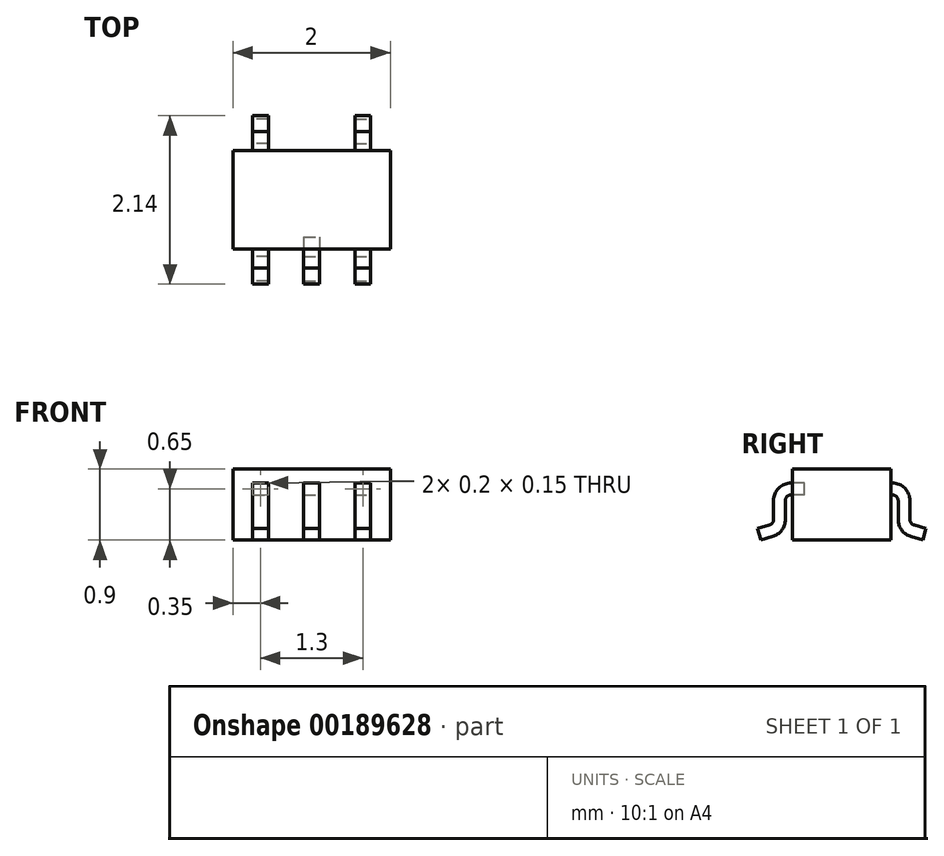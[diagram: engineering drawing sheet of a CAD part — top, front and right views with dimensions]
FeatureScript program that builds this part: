
annotation { "Feature Type Name" : "Feature", "Feature Type Description" : "" }
export const myFeature = defineFeature(function(context is Context, id is Id, definition is map)
    precondition{}
    {
        {
            var Q0;
            Q0=qCreatedBy(makeId("Top.planeOp"),FACE);
            var sketch = newSketch(context, id + "F0", { "sketchPlane" : qUnion([Q0])});
            skLineSegment(sketch, "E0.bottom", {"start": v(1, 0.62) * mm, "end": v(-1, 0.62) * mm});
            skLineSegment(sketch, "E0.top", {"start": v(1, -0.63) * mm, "end": v(-1, -0.63) * mm});
            skLineSegment(sketch, "E0.left", {"start": v(1, 0.62) * mm, "end": v(1, -0.63) * mm});
            skLineSegment(sketch, "E0.right", {"start": v(-1, 0.62) * mm, "end": v(-1, -0.63) * mm});
            skPoint(sketch, "E0.middle", {"position": v(0, 0) * mm});
            skSolve(sketch);
        }
        {
            var Q0;
            Q0=qSketchRegion(id+"F0",true);
            extrude(context, id + "F1", {"entities" : qUnion([Q0]), "depth" : 0.9 * mm});
        }
        {
            var Q0;
            Q0=qCreatedBy(makeId("Right.planeOp"),FACE);
            var sketch = newSketch(context, id + "F2", { "sketchPlane" : qUnion([Q0])});
            skLineSegment(sketch, "E1", {"start": v(-0.47, 0.65) * mm, "end": v(-0.64, 0.65) * mm});
            skLineSegment(sketch, "E2", {"start": v(-0.8, 0.5) * mm, "end": v(-0.8, 0.26) * mm});
            skLineSegment(sketch, "E3", {"start": v(-0.9, 0.12) * mm, "end": v(-1.05, 0.07) * mm});
            skPoint(sketch, "E4.visualSharp", {"position": v(-0.8, 0.65) * mm});
            skArc(sketch, "E4.filletArc", {"start": v(-0.64, 0.65) * mm, "mid": v(-0.75, 0.6) * mm, "end": v(-0.8, 0.5) * mm});
            skPoint(sketch, "E5.visualSharp", {"position": v(-0.8, 0.15) * mm});
            skArc(sketch, "E5.filletArc", {"start": v(-0.9, 0.12) * mm, "mid": v(-0.82, 0.17) * mm, "end": v(-0.8, 0.26) * mm});
            skSolve(sketch);
        }
        {
            var Q0;
            Q0=sQuery(id+"F2.wireOp",EDGE,"E1");
            var Q1;
            Q1=sQuery(id+"F2.wireOp",VERTEX,"E1.start");
            cPlane(context, id + "F3", {"entities" : qUnion([Q0, Q1]), "cplaneType" : CPlaneType.CURVE_POINT, "offset" : 150 * mm, "width" : 150 * mm, "height" : 150 * mm});
        }
        {
            var Q0;
            Q0=qCreatedBy(id+"F3.planeOp",FACE);
            var sketch = newSketch(context, id + "F4", { "sketchPlane" : qUnion([Q0])});
            skLineSegment(sketch, "E6.bottom", {"start": v(-0.1, 0.58) * mm, "end": v(0.1, 0.58) * mm});
            skLineSegment(sketch, "E6.top", {"start": v(-0.1, 0.73) * mm, "end": v(0.1, 0.73) * mm});
            skLineSegment(sketch, "E6.left", {"start": v(-0.1, 0.58) * mm, "end": v(-0.1, 0.73) * mm});
            skLineSegment(sketch, "E6.right", {"start": v(0.1, 0.58) * mm, "end": v(0.1, 0.73) * mm});
            skPoint(sketch, "E6.middle", {"position": v(0, 0.65) * mm});
            skSolve(sketch);
        }
        {
            var Q0;
            Q0=qSketchRegion(id+"F4",true);
            var Q1;
            Q1=qConstructionFilter(qBodyType(qCreatedBy(id+"F2",EDGE),BodyType.WIRE),ConstructionObject.NO);
            sweep(context, id + "F5", {"profiles" : qUnion([Q0]), "path" : qUnion([Q1])});
        }
        {
            var Q0;
            Q0=makeQuery(id+"F5.opSweep","SWEPT_BODY",BODY,{"disambiguationData":[OSD([sQuery(id+"F2.wireOp",EDGE,"E1"),sQuery(id+"F4.wireOp",EDGE,"E6.bottom"),sQuery(id+"F4.wireOp",EDGE,"E6.top"),sQuery(id+"F4.wireOp",EDGE,"E6.left"),sQuery(id+"F4.wireOp",EDGE,"E6.right")])]});
            transform(context, id + "F6", {"entities" : qUnion([Q0]), "transformType" : TransformType.TRANSLATION_3D, "dx" : 0.65 * mm, "dy" : 0 * mm, "dz" : 0 * mm, "makeCopy" : true});
        }
        {
            var Q0;
            Q0=makeQuery(id+"F6.opPattern","COPY",BODY,{"derivedFrom":makeQuery(id+"F5.opSweep","SWEPT_BODY",BODY,{"disambiguationData":[OSD([sQuery(id+"F2.wireOp",EDGE,"E1"),sQuery(id+"F4.wireOp",EDGE,"E6.bottom"),sQuery(id+"F4.wireOp",EDGE,"E6.top"),sQuery(id+"F4.wireOp",EDGE,"E6.left"),sQuery(id+"F4.wireOp",EDGE,"E6.right")])]}),"instanceName":"1"});
            var Q1;
            Q1=qCreatedBy(makeId("Right.planeOp"),FACE);
            mirror(context, id + "F7", {"entities" : qUnion([Q0]), "mirrorPlane" : qUnion([Q1])});
        }
        {
            var Q0;
            Q0=makeQuery(id+"F7.opPattern","COPY",BODY,{"derivedFrom":makeQuery(id+"F6.opPattern","COPY",BODY,{"derivedFrom":makeQuery(id+"F5.opSweep","SWEPT_BODY",BODY,{"disambiguationData":[OSD([sQuery(id+"F2.wireOp",EDGE,"E1"),sQuery(id+"F4.wireOp",EDGE,"E6.bottom"),sQuery(id+"F4.wireOp",EDGE,"E6.top"),sQuery(id+"F4.wireOp",EDGE,"E6.left"),sQuery(id+"F4.wireOp",EDGE,"E6.right")])]}),"instanceName":"1"}),"instanceName":"1"});
            var Q1;
            Q1=makeQuery(id+"F6.opPattern","COPY",BODY,{"derivedFrom":makeQuery(id+"F5.opSweep","SWEPT_BODY",BODY,{"disambiguationData":[OSD([sQuery(id+"F2.wireOp",EDGE,"E1"),sQuery(id+"F4.wireOp",EDGE,"E6.bottom"),sQuery(id+"F4.wireOp",EDGE,"E6.top"),sQuery(id+"F4.wireOp",EDGE,"E6.left"),sQuery(id+"F4.wireOp",EDGE,"E6.right")])]}),"instanceName":"1"});
            var Q2;
            Q2=qCreatedBy(makeId("Front.planeOp"),FACE);
            mirror(context, id + "F8", {"operationType" : NewBodyOperationType.ADD, "entities" : qUnion([Q0, Q1]), "mirrorPlane" : qUnion([Q2])});
        }
    });
